# Revit family: Seat-WCSeat-Duroplast-Vitra-EqualSeries_119-003-001
name_source: partatom
category: Plumbing Fixtures
revit_build: Autodesk Revit 2017 (Build: 20160225_1515(x64)
units: mm (PartAtom-declared; Revit-internal decimal feet)

## family parameters
Cut with Voids When Loaded = No
Host = Face
OmniClass Number = 23.45.05.21
OmniClass Title = Plumbing Fixtures - Sanitary Disposal Units
Part Type = Normal
Room Calculation Point = No
Round Connector Dimension = Use Diameter
Shared = Yes

## types (3) — shared parameters
BIMobject category = Sanitary - Toilet Seats
CW Connection = No
Color = White
Default Elevation = 410 mm  [stored 1.34514 ft]
Design country = Turkey
HW Connection = No
IFC Classification = Sanitary Terminal
Main Material = Duroplast
Manufacturer = Vitra
Manufacturer name = Vitra
NBS Referans Code = 35-93-95
NBS Referans Description = Wc Seats And Covers
Nominal Depth (mm) = 473 mm  [stored 1.55184 ft]
Nominal Height (mm) = 45 mm  [stored 0.147638 ft]
Nominal Width (mm) = 394 mm
OmniClass Code = 23-31 19 19 11
OmniClass Description = Toilets
Product certification = https://vitraglobal.com
Product family = Equal
Product url = https://www.vitraglobal.com
Secondary Material = White
Technical description = https://www.vitraglobal.com
UNSPSC Code = 35-93-95
UNSPSC Description = Water Operated Water Closets
URL = https://www.vitra.com.tr
Uniclass 1.4 Code = L72164
Uniclass 1.4 Description = Toilets
Uniclass 2.0 Code = PR-35-93-95
Uniclass 2.0 Description = Wc Seats And Covers
Uniclass 2015 Code = Pr_40_20_93_95
Uniclass 2015 Name = WC seats and covers
Vent Connection = No
Warranty Period (Year) = 2 Years
Waste Connection = No
Weight Net (kg) = 3
Youtube = https://www.youtube.com
zero-valued in all types: Cost

## per-type parameters (varying)
| type | Article No. (default) | Description | Model | Product Manual | Product SKU |
| Seat-WCSeat-Duroplast, Metal hinge, top fixing-119-003-001 | 119-003-001 | VitrA Equal WC Seat | 119-003-001 | Seat-WCSeat-Duroplast, Metal hinge, top fixing | 119-003-001 |
| Seat-WCSeat-Duroplast, Metal hinge, top fixing-soft close-119-003-009 | 119-003-009 | VitrA Equal WC Seat - Soft Close | 119-003-009 | Seat-WCSeat-Duroplast, Metal hinge, top fixing, soft close | 119-003-009 |
| Seat-WCSeat-Duroplast, Metal hinge, top fixing-soft close-quick release-119-003R009 | 119-003R009 | VitrA Equal WC Seat - Soft Close- quick release | 119-003R009 | Seat-WCSeat-Duroplast, Metal hinge, top fixing, soft close-quick release | 119-003R009 |

note: [stored X ft] marks values corroborated as IEEE doubles in the binary element streams (Revit-internal decimal feet)

## geometry (parser evidence)
native form markers: Sweep x3
no freeform markers — native parametric forms only
